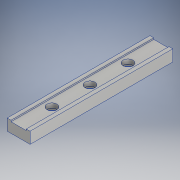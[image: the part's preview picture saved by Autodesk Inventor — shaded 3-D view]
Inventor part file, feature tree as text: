
AUTODESK INVENTOR PART (.ipt)
format: ipt  version: 2019 (Build 230136000, 136)  size: 129,536 bytes
history: native  units: mm
features: other x3, extrude x1, hole x1
ambient origin geometry x8: Origin, YZ Plane, XZ Plane, XY Plane, X Axis, Y Axis, Z Axis, Center Point
bodies: Solid1 (feature_tree), Body (feature_tree)
feature tree (5):
  extrude  "Clamp Cutout"  Depth=75.0mm
  hole  "Fastening Holes"  [1 undecoded]
  other  "Body Outline"
  other  "Clamp Cutout Outline"
  other  "Fastening Hole Positions"
note: 1 required parameter value undecoded (feature->parameter linkage not recoverable at this tier; creation-order binding heuristic only, values carry confidence <= 0.55)
